# Revit family: 210_6c4e02319ab34752af79770a1d07d9
name_source: partatom
category: Mechanical Equipment
revit_build: Autodesk Revit 2018 (Build: 20170223_1515(x64)
units: mm (PartAtom-declared; Revit-internal decimal feet)

## family parameters
Always vertical = Yes
Cut with Voids When Loaded = No
Part Type = Breaks Into
Room Calculation Point = No
Round Connector Dimension = Use Diameter
Shared = No
Work Plane-Based = No

## types (1)
- UNI 2 REL (700085)
    CAT0 = Yes
    Clearance Zone Front Depth = 790 mm  [stored 2.59186 ft]
    DEXH = 125 mm
    DEXT = 125 mm
    DEXT9 = 125 mm
    DL = 48 mm  [stored 0.15748 ft]
    DOUT = 125 mm
    DSUP = 125 mm
    Description = UNI 2 REL (700085)
    EXHX = 95 mm  [stored 0.31168 ft]
    EXHY = 110 mm  [stored 0.360892 ft]
    EXT9X = 0 mm  [stored 0 ft]
    EXT9Y = 280 mm  [stored 0.918635 ft]
    EXTX = 216 mm  [stored 0.708661 ft]
    EXTY = 241 mm  [stored 0.790682 ft]
    H = 703 mm  [stored 2.30643 ft]
    H2 = 352 mm
    L2 = 316 mm  [stored 1.03675 ft]
    MC Product Code = UNI 2 REL (700085)
    Manufacturer = Flexit
    OUTX = 95 mm  [stored 0.31168 ft]
    OUTY = 110 mm  [stored 0.360892 ft]
    QmdConnectorList = 221;DSUP;231;DOUT;241;DEXT;249;DEXT9;251;DEXH
    REXH = 63 mm
    REXT = 63 mm
    REXT9 = 63 mm
    ROUT = 63 mm
    RSUP = 63 mm
    SUPX = 216 mm  [stored 0.708661 ft]
    SUPY = 241 mm  [stored 0.790682 ft]
    W = 408 mm  [stored 1.33858 ft]
    magiPartTypeId = 210
    magiProductFamilyId = 6c4e02319ab34752af79770a1d07d9
    magiProductId = 6c4e02319ab34752af79770a1d07d9

note: [stored X ft] marks values corroborated as IEEE doubles in the binary element streams (Revit-internal decimal feet)

## geometry (parser evidence)
native form markers: Sweep x1
no freeform markers — native parametric forms only
